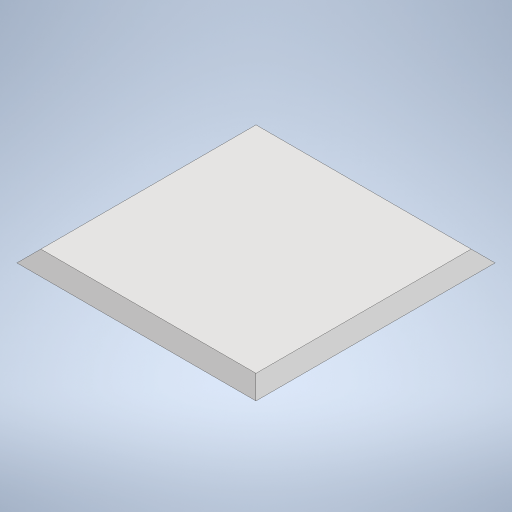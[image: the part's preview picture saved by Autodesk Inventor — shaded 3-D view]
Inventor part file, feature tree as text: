
AUTODESK INVENTOR PART (.ipt)
format: ipt  version: 2024.1 (Build 281209000, 209)  size: 205,312 bytes
history: native  units: mm
features: extrude x1, chamfer x1, sketch x1
ambient origin geometry x8: Origin, YZ Plane, XZ Plane, XY Plane, X Axis, Y Axis, Z Axis, Center Point
bodies: Solid1 (feature_tree)
feature tree (3):
  extrude  "Extrusion1"  Depth=10.0mm
  chamfer  "Chamfer1"  Distance=10.0mm
  sketch  "Sketch1"  dims[d0=200.0mm d1=200.0mm d2=10.0mm d3=0.0mm d4=10.0mm d5=2.0mm d6=45.0deg]
